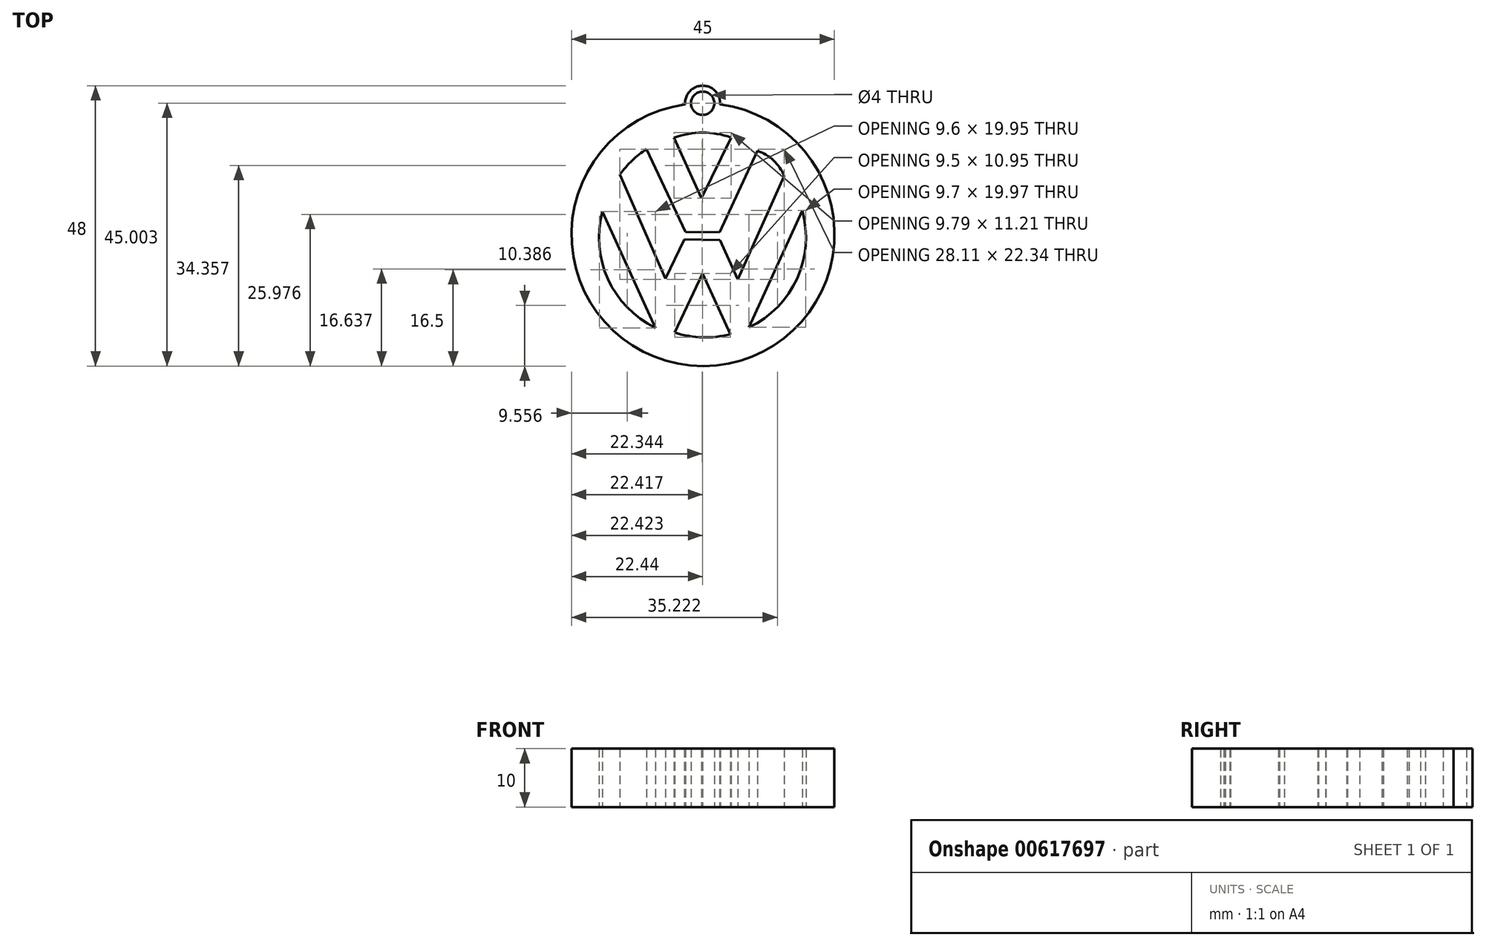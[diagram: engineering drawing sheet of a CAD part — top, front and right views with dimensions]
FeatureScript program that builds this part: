
annotation { "Feature Type Name" : "Feature", "Feature Type Description" : "" }
export const myFeature = defineFeature(function(context is Context, id is Id, definition is map)
    precondition{}
    {
        {
            var Q0;
            Q0=qCreatedBy(makeId("Top.planeOp"),FACE);
            var sketch = newSketch(context, id + "F0", { "sketchPlane" : qUnion([Q0])});
            skLineSegment(sketch, "E0", {"start": v(0, 0) * mm, "end": v(0.06, 0.2) * mm});
            skLineSegment(sketch, "E1", {"start": v(0, 0) * mm, "end": v(-0.08, 0.28) * mm});
            skArc(sketch, "E2", {"start": v(4.87, 16.8) * mm, "mid": v(-0.02, 17.65) * mm, "end": v(-4.92, 16.8) * mm});
            skLineSegment(sketch, "E3", {"start": v(0, 0) * mm, "end": v(-0.2, 0.3) * mm});
            skLineSegment(sketch, "E4", {"start": v(0, 0) * mm, "end": v(-0.51, 0.38) * mm});
            skArc(sketch, "E5", {"start": v(-9.62, 14.84) * mm, "mid": v(-12.08, 12.87) * mm, "end": v(-14.15, 10.49) * mm});
            skLineSegment(sketch, "E6", {"start": v(0.02, 0.26) * mm, "end": v(-0.51, 0.38) * mm});
            skLineSegment(sketch, "E7", {"start": v(0.02, 0.26) * mm, "end": v(-0.08, 0.06) * mm});
            skArc(sketch, "E8", {"start": v(-17.15, 4.17) * mm, "mid": v(-16.2, -7.44) * mm, "end": v(-8.08, -15.79) * mm});
            skLineSegment(sketch, "E9", {"start": v(0.02, 0.26) * mm, "end": v(-0.04, 0.03) * mm});
            skArc(sketch, "E10", {"start": v(-4.77, -16.57) * mm, "mid": v(-0.04, -17.4) * mm, "end": v(4.73, -16.85) * mm});
            skLineSegment(sketch, "E11", {"start": v(0.02, 0.26) * mm, "end": v(0.14, 0.03) * mm});
            skLineSegment(sketch, "E12", {"start": v(0, 0) * mm, "end": v(0.14, 0.03) * mm});
            skArc(sketch, "E13", {"start": v(7.93, -15.66) * mm, "mid": v(16.15, -7.34) * mm, "end": v(17.04, 4.31) * mm});
            skLineSegment(sketch, "E14", {"start": v(0, 0) * mm, "end": v(0.11, 0.08) * mm});
            skArc(sketch, "E15", {"start": v(13.96, 10.24) * mm, "mid": v(12.14, 12.88) * mm, "end": v(9.4, 14.54) * mm});
            skArc(sketch, "E16", {"start": v(-3, 22.49) * mm, "mid": v(0.11, -22.3) * mm, "end": v(3, 22.5) * mm});
            skLineSegment(sketch, "E17", {"start": v(-17.15, 4.17) * mm, "end": v(-8.08, -15.79) * mm});
            skLineSegment(sketch, "E18", {"start": v(0, -6.45) * mm, "end": v(4.73, -16.85) * mm});
            skLineSegment(sketch, "E19", {"start": v(0, -6.45) * mm, "end": v(-4.77, -16.57) * mm});
            skLineSegment(sketch, "E20", {"start": v(17.04, 4.31) * mm, "end": v(7.93, -15.66) * mm});
            skLineSegment(sketch, "E21", {"start": v(-4.92, 16.8) * mm, "end": v(-0.2, 6.44) * mm});
            skLineSegment(sketch, "E22", {"start": v(4.87, 16.8) * mm, "end": v(-0.2, 6.44) * mm});
            skLineSegment(sketch, "E23", {"start": v(-14.15, 10.49) * mm, "end": v(-6.38, -7.33) * mm});
            skLineSegment(sketch, "E24", {"start": v(13.96, 10.24) * mm, "end": v(6.03, -7.5) * mm});
            skLineSegment(sketch, "E25", {"start": v(-6.38, -7.33) * mm, "end": v(-3.15, -0.64) * mm});
            skLineSegment(sketch, "E26", {"start": v(6.03, -7.5) * mm, "end": v(2.96, -0.74) * mm});
            skLineSegment(sketch, "E27", {"start": v(2.96, -0.74) * mm, "end": v(-3.15, -0.64) * mm});
            skPoint(sketch, "E28.end.orphan", {"position": v(-2.87, 0) * mm});
            skLineSegment(sketch, "E29", {"start": v(9.4, 14.54) * mm, "end": v(2.9, 0.6) * mm});
            skLineSegment(sketch, "E30", {"start": v(-9.62, 14.84) * mm, "end": v(-2.93, 0.63) * mm});
            skLineSegment(sketch, "E31", {"start": v(-2.93, 0.63) * mm, "end": v(2.9, 0.6) * mm});
            skCircle(sketch, "E32", {"center": v(0, 22.7) * mm, "radius": 2 * mm});
            skArc(sketch, "E33", {"start": v(3, 22.5) * mm, "mid": v(0, 25.7) * mm, "end": v(-3, 22.49) * mm});
            skSolve(sketch);
        }
        {
            var Q0;
            Q0 = qSketchRegion(id + "F0", true);
            extrude(context, id + "F1", {"entities" : qUnion([Q0]), "depth" : 10 * mm, "offsetDistance" : 25 * mm});
        }
    });
